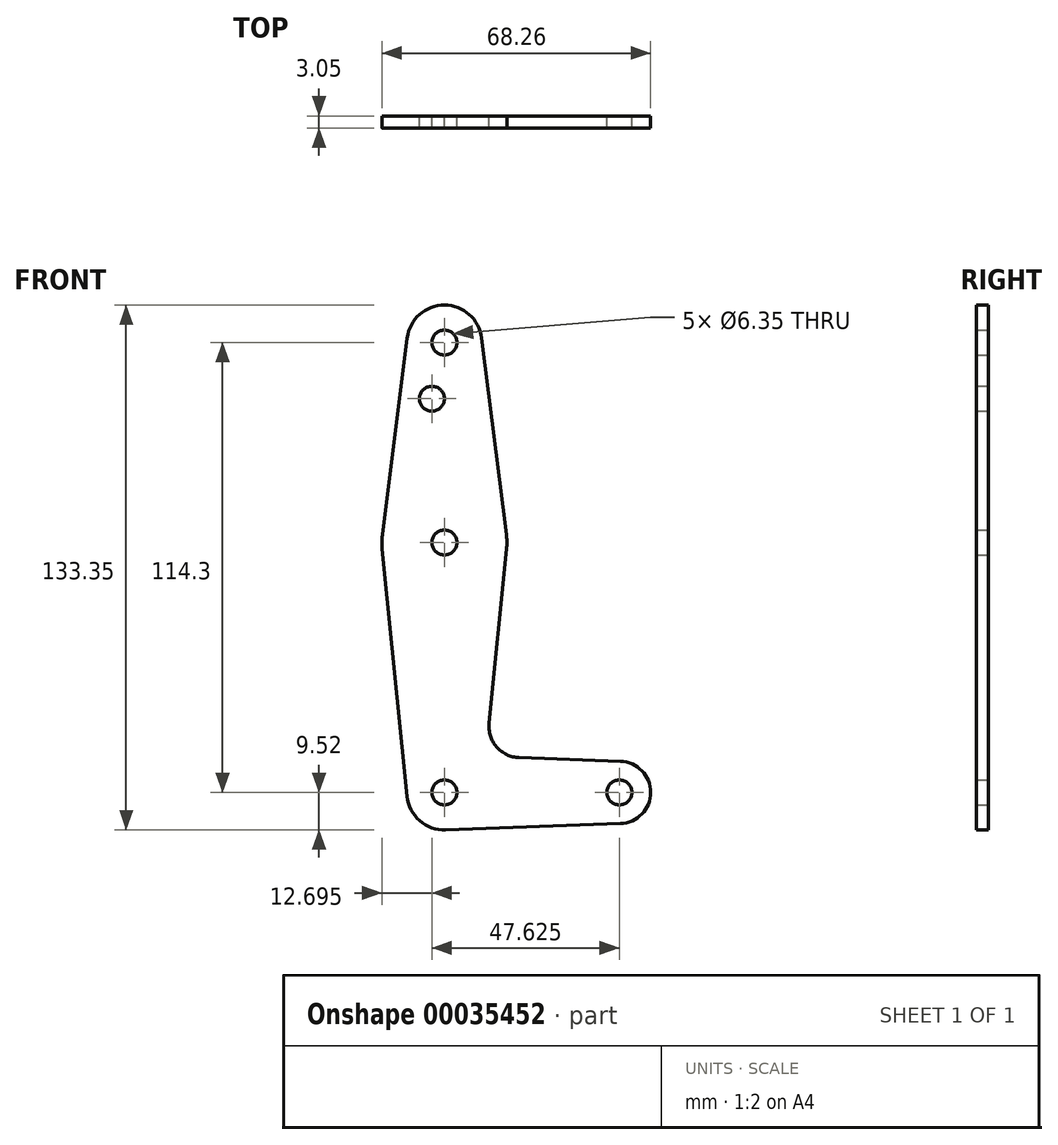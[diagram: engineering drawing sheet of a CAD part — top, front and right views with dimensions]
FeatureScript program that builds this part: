
annotation { "Feature Type Name" : "Feature", "Feature Type Description" : "" }
export const myFeature = defineFeature(function(context is Context, id is Id, definition is map)
    precondition{}
    {
        {
            var Q0;
            Q0=qCreatedBy(makeId("Front.planeOp"),FACE);
            var sketch = newSketch(context, id + "F0", { "sketchPlane" : qUnion([Q0])});
            skLineSegment(sketch, "E0", {"start": v(0, 0) * mm, "end": v(0, 114.3) * mm, "construction": true});
            skLineSegment(sketch, "E1", {"start": v(0, 0) * mm, "end": v(44.45, 0) * mm, "construction": true});
            skCircle(sketch, "E2", {"center": v(0, 114.3) * mm, "radius": 9.53 * mm});
            skCircle(sketch, "E3", {"center": v(0, 63.5) * mm, "radius": 15.88 * mm});
            skCircle(sketch, "E4", {"center": v(0, 0) * mm, "radius": 9.53 * mm});
            skCircle(sketch, "E5", {"center": v(44.45, 0) * mm, "radius": 7.94 * mm});
            skLineSegment(sketch, "E6", {"start": v(-9.45, 115.5) * mm, "end": v(-15.75, 65.48) * mm});
            skLineSegment(sketch, "E7", {"start": v(-9.48, -0.95) * mm, "end": v(-15.8, 61.91) * mm});
            skLineSegment(sketch, "E8", {"start": v(9.45, 115.5) * mm, "end": v(15.75, 65.48) * mm});
            skLineSegment(sketch, "E9", {"start": v(15.8, 61.91) * mm, "end": v(11.34, 17.6) * mm});
            skLineSegment(sketch, "E10", {"start": v(0.34, -9.52) * mm, "end": v(44.73, -7.93) * mm});
            skLineSegment(sketch, "E11", {"start": v(18.97, 8.85) * mm, "end": v(44.73, 7.93) * mm});
            skCircle(sketch, "E12", {"center": v(0, 114.3) * mm, "radius": 3.18 * mm});
            skCircle(sketch, "E13", {"center": v(0, 63.5) * mm, "radius": 3.18 * mm});
            skCircle(sketch, "E14", {"center": v(0, 0) * mm, "radius": 3.18 * mm});
            skCircle(sketch, "E15", {"center": v(44.45, 0) * mm, "radius": 3.18 * mm});
            skCircle(sketch, "E16", {"center": v(-3.18, 100.03) * mm, "radius": 3.18 * mm});
            skArc(sketch, "E17.filletArc", {"start": v(11.34, 17.6) * mm, "mid": v(13.26, 11.57) * mm, "end": v(18.97, 8.85) * mm});
            skSolve(sketch);
        }
        {
            var Q0;
            Q0 = qSketchRegion(id + "F0", true);
            extrude(context, id + "F1", {"entities" : qUnion([Q0]), "depth" : 3.05 * mm});
        }
    });
